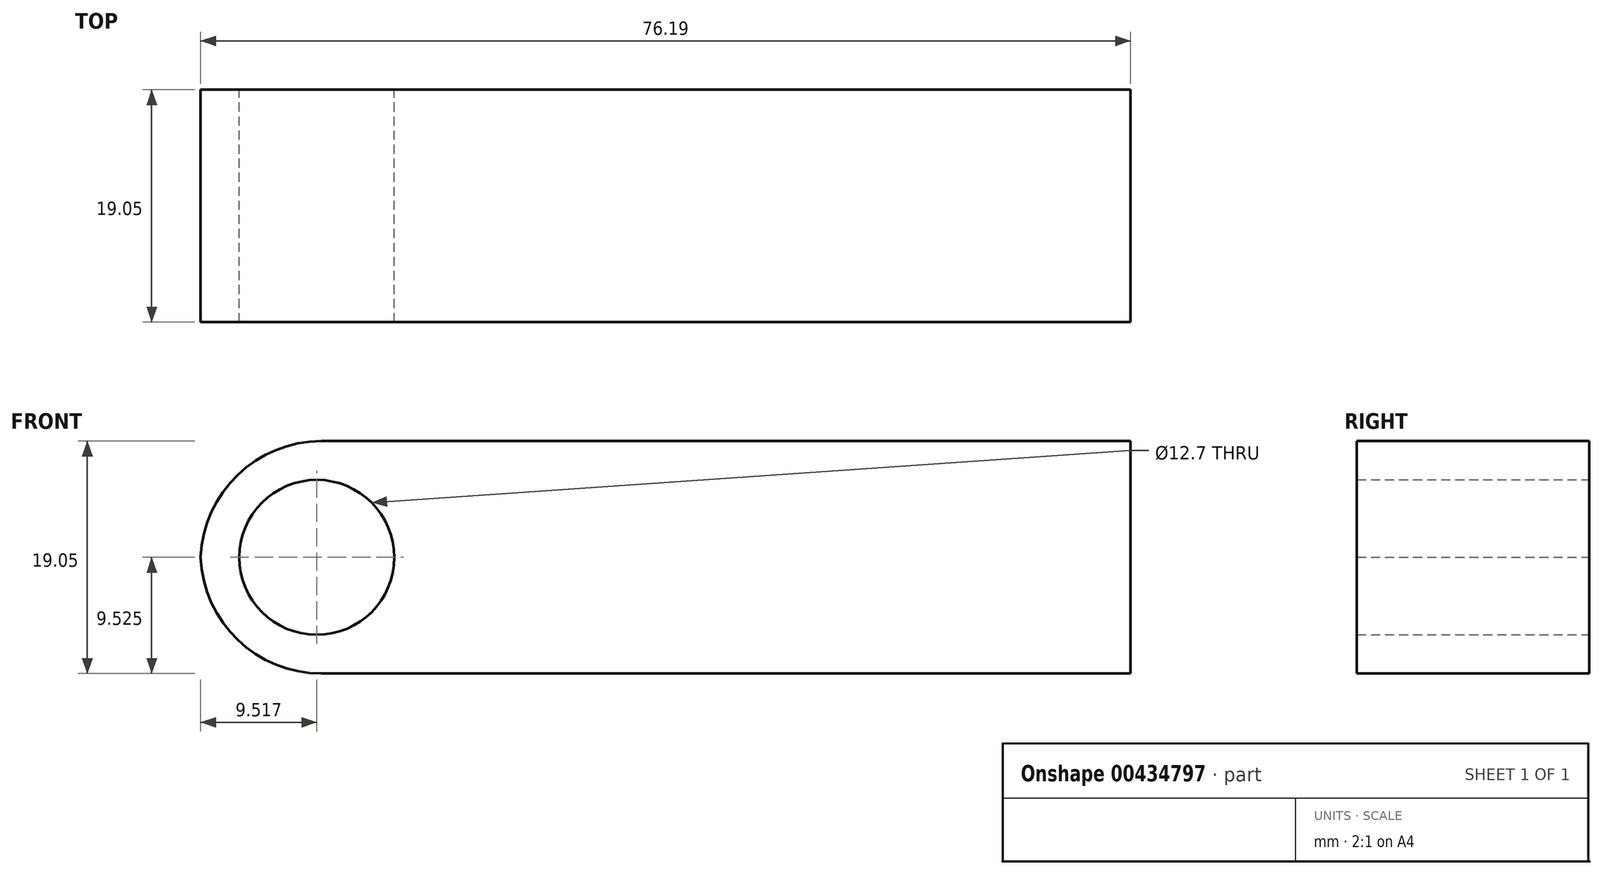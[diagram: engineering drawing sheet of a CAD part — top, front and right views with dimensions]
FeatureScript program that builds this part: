
annotation { "Feature Type Name" : "Feature", "Feature Type Description" : "" }
export const myFeature = defineFeature(function(context is Context, id is Id, definition is map)
    precondition{}
    {
        {
            var Q0;
            Q0=qCreatedBy(makeId("Top.planeOp"),FACE);
            var sketch = newSketch(context, id + "F0", { "sketchPlane" : qUnion([Q0])});
            skLineSegment(sketch, "E0.bottom", {"start": v(-28.48, 5.03) * mm, "end": v(47.72, 5.03) * mm});
            skLineSegment(sketch, "E0.top", {"start": v(-28.48, -14.02) * mm, "end": v(47.72, -14.02) * mm});
            skLineSegment(sketch, "E0.left", {"start": v(-28.48, 5.03) * mm, "end": v(-28.48, -14.02) * mm});
            skLineSegment(sketch, "E0.right", {"start": v(47.72, 5.03) * mm, "end": v(47.72, -14.02) * mm});
            skSolve(sketch);
        }
        {
            var Q0;
            Q0=makeQuery(id+"F0.imprint","IMPRINT",FACE,{"disambiguationData":[TD([[makeQuery(id+"F0.imprint","IMPRINT",EDGE,{"derivedFrom":sQuery(id+"F0.wireOp",EDGE,"E0.bottom")}),-1.0]])]});
            extrude(context, id + "F1", {"entities" : qUnion([Q0]), "depth" : 19.05 * mm});
        }
        {
            var Q0;
            Q0=makeQuery(id+"F1.opExtrude","SWEPT_FACE",FACE,{"disambiguationData":[OSD([sQuery(id+"F0.wireOp",EDGE,"E0.bottom")])]});
            var sketch = newSketch(context, id + "F2", { "sketchPlane" : qUnion([Q0])});
            skPoint(sketch, "E1", {"position": v(18.95, 9.53) * mm});
            skSolve(sketch);
        }
        {
            var Q0;
            Q0=sQuery(id+"F2.wireOp",VERTEX,"E1");
            var Q1;
            Q1=makeQuery(id+"F1.opExtrude","SWEPT_BODY",BODY,{"disambiguationData":[OSD([sQuery(id+"F0.wireOp",EDGE,"E0.bottom"),sQuery(id+"F0.wireOp",EDGE,"E0.top"),sQuery(id+"F0.wireOp",EDGE,"E0.left"),sQuery(id+"F0.wireOp",EDGE,"E0.right")])]});
            hole(context, id + "F3", {"style" : HoleStyle.SIMPLE, "endStyle" : HoleEndStyle.THROUGH, "holeDiameter" : 12.7 * mm, "isTappedThrough" : true, "tappedDepth" : 12.7 * mm, "tapClearance" : 3, "locations" : qUnion([Q0]), "scope" : qUnion([Q1])});
        }
        {
            var Q0;
            Q0=makeQuery(id+"F1.opExtrude","CAP_EDGE",EDGE,{"disambiguationData":[OSD([sQuery(id+"F0.wireOp",EDGE,"E0.left")])],"isStart":false});
            var Q1;
            Q1=makeQuery(id+"F1.opExtrude","CAP_EDGE",EDGE,{"disambiguationData":[OSD([sQuery(id+"F0.wireOp",EDGE,"E0.left")])],"isStart":true});
            fillet(context, id + "F4", {"entities" : qUnion([Q0, Q1]), "radius" : 9.9 * mm, "tangentPropagation" : true, "allowEdgeOverflow" : false});
        }
    });
